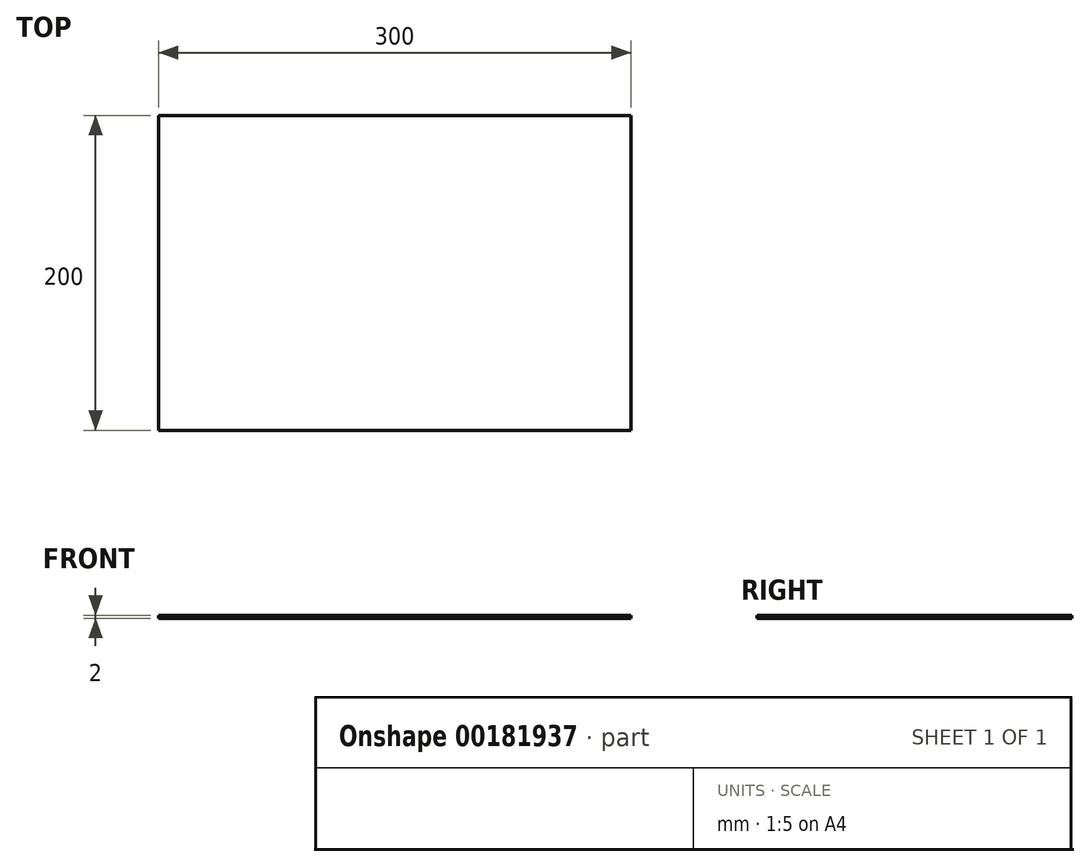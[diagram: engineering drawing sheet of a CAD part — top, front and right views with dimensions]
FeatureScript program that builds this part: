
annotation { "Feature Type Name" : "Feature", "Feature Type Description" : "" }
export const myFeature = defineFeature(function(context is Context, id is Id, definition is map)
    precondition{}
    {
        {
            var Q0;
            Q0=qCreatedBy(makeId("Top.planeOp"),FACE);
            var sketch = newSketch(context, id + "F0", { "sketchPlane" : qUnion([Q0])});
            skLineSegment(sketch, "E0.bottom", {"start": v(-300, 200) * mm, "end": v(0, 200) * mm});
            skLineSegment(sketch, "E0.top", {"start": v(-300, 0) * mm, "end": v(0, 0) * mm});
            skLineSegment(sketch, "E0.left", {"start": v(-300, 200) * mm, "end": v(-300, 0) * mm});
            skLineSegment(sketch, "E0.right", {"start": v(0, 200) * mm, "end": v(0, 0) * mm});
            skSolve(sketch);
        }
        {
            var Q0;
            Q0 = qSketchRegion(id + "F0", true);
            extrude(context, id + "F1", {"entities" : qUnion([Q0]), "depth" : 2 * mm});
        }
    });
